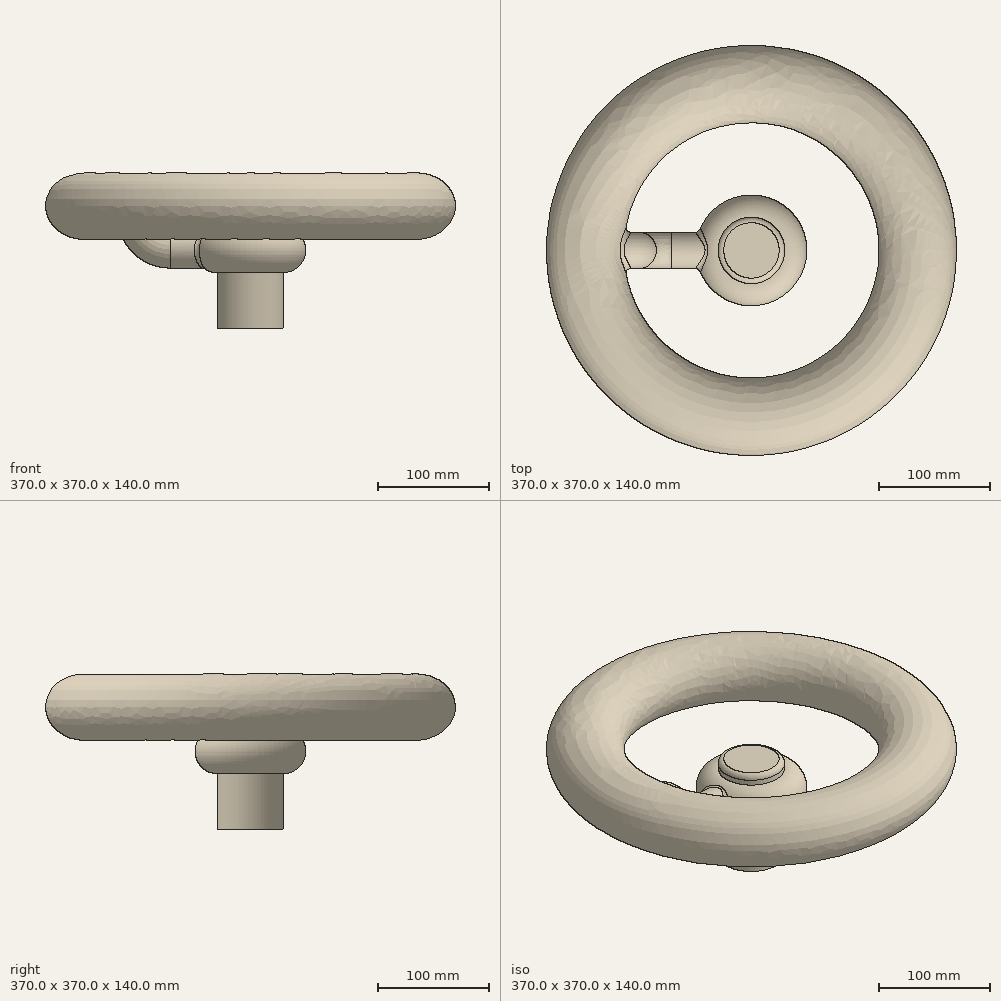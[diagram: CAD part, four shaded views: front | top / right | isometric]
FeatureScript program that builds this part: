
annotation { "Feature Type Name" : "Feature", "Feature Type Description" : "" }
export const myFeature = defineFeature(function(context is Context, id is Id, definition is map)
    precondition{}
    {
        {
            var Q0;
            Q0=qCreatedBy(makeId("Front.planeOp"),FACE);
            var sketch = newSketch(context, id + "F0", { "sketchPlane" : qUnion([Q0])});
            skLineSegment(sketch, "E0.bottom", {"start": v(0, 0) * mm, "end": v(-30, 0) * mm});
            skLineSegment(sketch, "E0.top", {"start": v(0, 100) * mm, "end": v(-30, 100) * mm});
            skLineSegment(sketch, "E0.left", {"start": v(0, 0) * mm, "end": v(0, 100) * mm});
            skLineSegment(sketch, "E0.right", {"start": v(-30, 0) * mm, "end": v(-30, 50) * mm});
            skArc(sketch, "E1", {"start": v(-30, 90) * mm, "mid": v(-50, 70) * mm, "end": v(-30, 50) * mm});
            skLineSegment(sketch, "E2.trimOffspring", {"start": v(-30, 90) * mm, "end": v(-30, 100) * mm});
            skSolve(sketch);
        }
        {
            var Q0;
            Q0=makeQuery(id+"F0.imprint","IMPRINT",FACE,{"disambiguationData":[TD([[makeQuery(id+"F0.imprint","IMPRINT",EDGE,{"derivedFrom":sQuery(id+"F0.wireOp",EDGE,"E0.bottom")}),-1.0]])]});
            var Q1;
            Q1=sQuery(id+"F0.wireOp",EDGE,"E0.left");
            revolve(context, id + "F1", {"entities" : qUnion([Q0]), "axis" : qUnion([Q1]), "revolveType" : RevolveType.FULL});
        }
        {
            var Q0;
            Q0=qCreatedBy(makeId("Front.planeOp"),FACE);
            var sketch = newSketch(context, id + "F2", { "sketchPlane" : qUnion([Q0])});
            skEllipse(sketch, "E3", {"center": v(-150, 110) * mm, "majorRadius": 35 * mm, "minorRadius": 30 * mm, "majorAxis": v(1, 0)});
            skLineSegment(sketch, "E4", {"start": v(0, 0) * mm, "end": v(0, 109.79) * mm, "construction": true});
            skSolve(sketch);
        }
        {
            var Q0;
            Q0=makeQuery(id+"F2.imprint","IMPRINT",FACE,{"disambiguationData":[TD([[makeQuery(id+"F2.imprint","IMPRINT",EDGE,{"derivedFrom":sQuery(id+"F2.wireOp",EDGE,"E3")}),1.0]])]});
            var Q1;
            Q1=sQuery(id+"F2.wireOp",EDGE,"E4");
            revolve(context, id + "F3", {"entities" : qUnion([Q0]), "axis" : qUnion([Q1]), "revolveType" : RevolveType.FULL});
        }
        {
            var Q0;
            Q0=qCreatedBy(makeId("Front.planeOp"),FACE);
            var sketch = newSketch(context, id + "F4", { "sketchPlane" : qUnion([Q0])});
            skLineSegment(sketch, "E5", {"start": v(-150, 110) * mm, "end": v(-120, 110) * mm});
            skArc(sketch, "E6", {"start": v(-96.39, 92.08) * mm, "mid": v(-86.9, 80.3) * mm, "end": v(-72.44, 75.87) * mm});
            skLineSegment(sketch, "E7", {"start": v(-72.44, 75.87) * mm, "end": v(0, 75.87) * mm});
            skArc(sketch, "E8", {"start": v(-96.39, 92.08) * mm, "mid": v(-105.18, 105.01) * mm, "end": v(-120, 110) * mm});
            skSolve(sketch);
        }
        {
            var Q0;
            Q0=qCreatedBy(makeId("Right.planeOp"),FACE);
            var sketch = newSketch(context, id + "F5", { "sketchPlane" : qUnion([Q0])});
            skCircle(sketch, "E9", {"center": v(0, 70.55) * mm, "radius": 16.44 * mm});
            skSolve(sketch);
        }
        {
            var Q0;
            Q0=qSketchRegion(id+"F5",true);
            var Q1;
            Q1=qConstructionFilter(qBodyType(qCreatedBy(id+"F4",EDGE),BodyType.WIRE),ConstructionObject.NO);
            sweep(context, id + "F6", {"operationType" : NewBodyOperationType.ADD, "profiles" : qUnion([Q0]), "path" : qUnion([Q1])});
        }
        {
            var Q0;
            Q0=makeQuery(id+"F6.boolean.opBoolean","INTERSECT",EDGE,{"derivedFrom":[makeQuery(id+"F1.opRevolve","SWEPT_FACE",FACE,{"disambiguationData":[OSD([sQuery(id+"F0.wireOp",EDGE,"E1")])]}),makeQuery(id+"F6.opSweep","SWEPT_FACE",FACE,{"disambiguationData":[OSD([sQuery(id+"F4.wireOp",EDGE,"E7"),sQuery(id+"F5.wireOp",EDGE,"E9")])]})]});
            var Q1;
            Q1=makeQuery(id+"F6.boolean.opBoolean","INTERSECT",EDGE,{"derivedFrom":[makeQuery(id+"F3.opRevolve","SWEPT_FACE",FACE,{"disambiguationData":[OSD([sQuery(id+"F2.wireOp",EDGE,"E3")])]}),makeQuery(id+"F6.opSweep","SWEPT_FACE",FACE,{"disambiguationData":[OSD([sQuery(id+"F4.wireOp",EDGE,"E8"),sQuery(id+"F5.wireOp",EDGE,"E9")])]})]});
            var Q2;
            Q2=makeQuery(id+"F6.boolean.opBoolean","INTERSECT",EDGE,{"derivedFrom":[makeQuery(id+"F3.opRevolve","SWEPT_FACE",FACE,{"disambiguationData":[OSD([sQuery(id+"F2.wireOp",EDGE,"E3")])]}),makeQuery(id+"F6.opSweep","SWEPT_FACE",FACE,{"disambiguationData":[OSD([sQuery(id+"F4.wireOp",EDGE,"E5"),sQuery(id+"F5.wireOp",EDGE,"E9")])]})]});
            var Q3;
            Q3=makeQuery(id+"F1.opRevolve","SWEPT_EDGE",EDGE,{"disambiguationData":[OSD([sQuery(id+"F0.wireOp",EDGE,"E0.top"),sQuery(id+"F0.wireOp",EDGE,"E2.trimOffspring")])]});
            fillet(context, id + "F7", {"entities" : qUnion([Q0, Q1, Q2, Q3]), "radius" : 5 * mm, "allowEdgeOverflow" : false});
        }
    });
